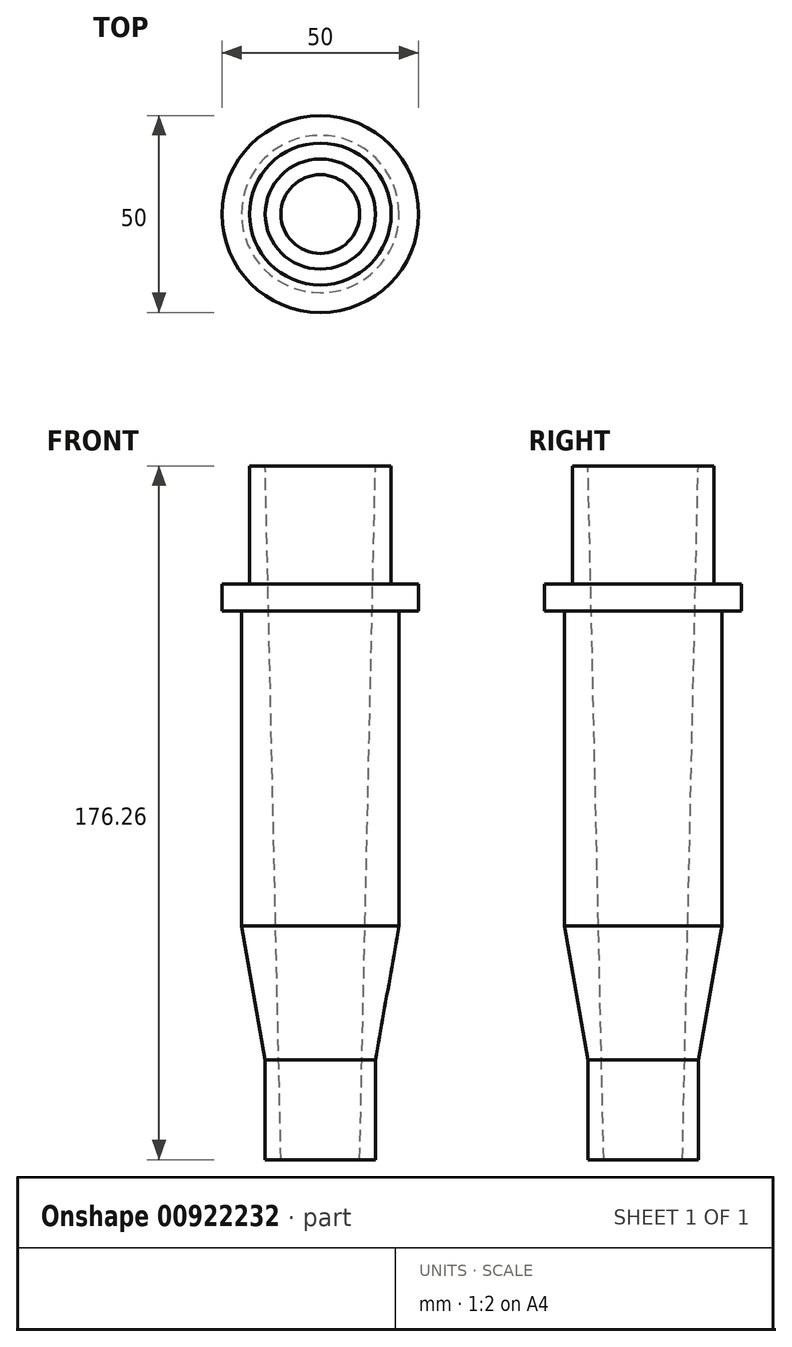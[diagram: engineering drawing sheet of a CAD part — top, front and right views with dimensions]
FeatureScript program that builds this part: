
annotation { "Feature Type Name" : "Feature", "Feature Type Description" : "" }
export const myFeature = defineFeature(function(context is Context, id is Id, definition is map)
    precondition{}
    {
        {
            var Q0;
            Q0=qCreatedBy(makeId("Front.planeOp"),FACE);
            var sketch = newSketch(context, id + "F0", { "sketchPlane" : qUnion([Q0])});
            skLineSegment(sketch, "E0", {"start": v(-14, 69.5) * mm, "end": v(-18, 69.5) * mm});
            skLineSegment(sketch, "E1", {"start": v(-18, 69.5) * mm, "end": v(-18, 39.5) * mm});
            skLineSegment(sketch, "E2", {"start": v(-10, -106.77) * mm, "end": v(-14, 69.5) * mm});
            skLineSegment(sketch, "E3", {"start": v(-20, 39.5) * mm, "end": v(-18, 39.5) * mm});
            skLineSegment(sketch, "E4", {"start": v(0, 77.75) * mm, "end": v(0, -122.25) * mm, "construction": true});
            skLineSegment(sketch, "E5", {"start": v(-14, -106.77) * mm, "end": v(-10, -106.77) * mm});
            skLineSegment(sketch, "E6", {"start": v(-20, -47.42) * mm, "end": v(-14, -81.45) * mm});
            skLineSegment(sketch, "E7", {"start": v(-14, -81.45) * mm, "end": v(-14, -106.77) * mm});
            skLineSegment(sketch, "E8", {"start": v(-10, -122.25) * mm, "end": v(-10, 77.75) * mm, "construction": true});
            skLineSegment(sketch, "E9", {"start": v(-10, -81.45) * mm, "end": v(-25.46, 6.24) * mm, "construction": true});
            skLineSegment(sketch, "E10", {"start": v(-20, -47.42) * mm, "end": v(-20, 32.58) * mm});
            skLineSegment(sketch, "E11", {"start": v(-20, 32.58) * mm, "end": v(-25, 32.58) * mm});
            skLineSegment(sketch, "E12", {"start": v(-25, 32.58) * mm, "end": v(-25, 39.5) * mm});
            skLineSegment(sketch, "E13", {"start": v(-25, 39.5) * mm, "end": v(-20, 39.5) * mm});
            skSolve(sketch);
        }
        {
            var Q0;
            Q0=qSketchRegion(id+"F0",true);
            var Q1;
            Q1=sQuery(id+"F0.wireOp",EDGE,"E4");
            revolve(context, id + "F1", {"surfaceOperationType" : NewSurfaceOperationType.NEW, "entities" : qUnion([Q0]), "axis" : qUnion([Q1]), "revolveType" : RevolveType.FULL});
        }
    });
